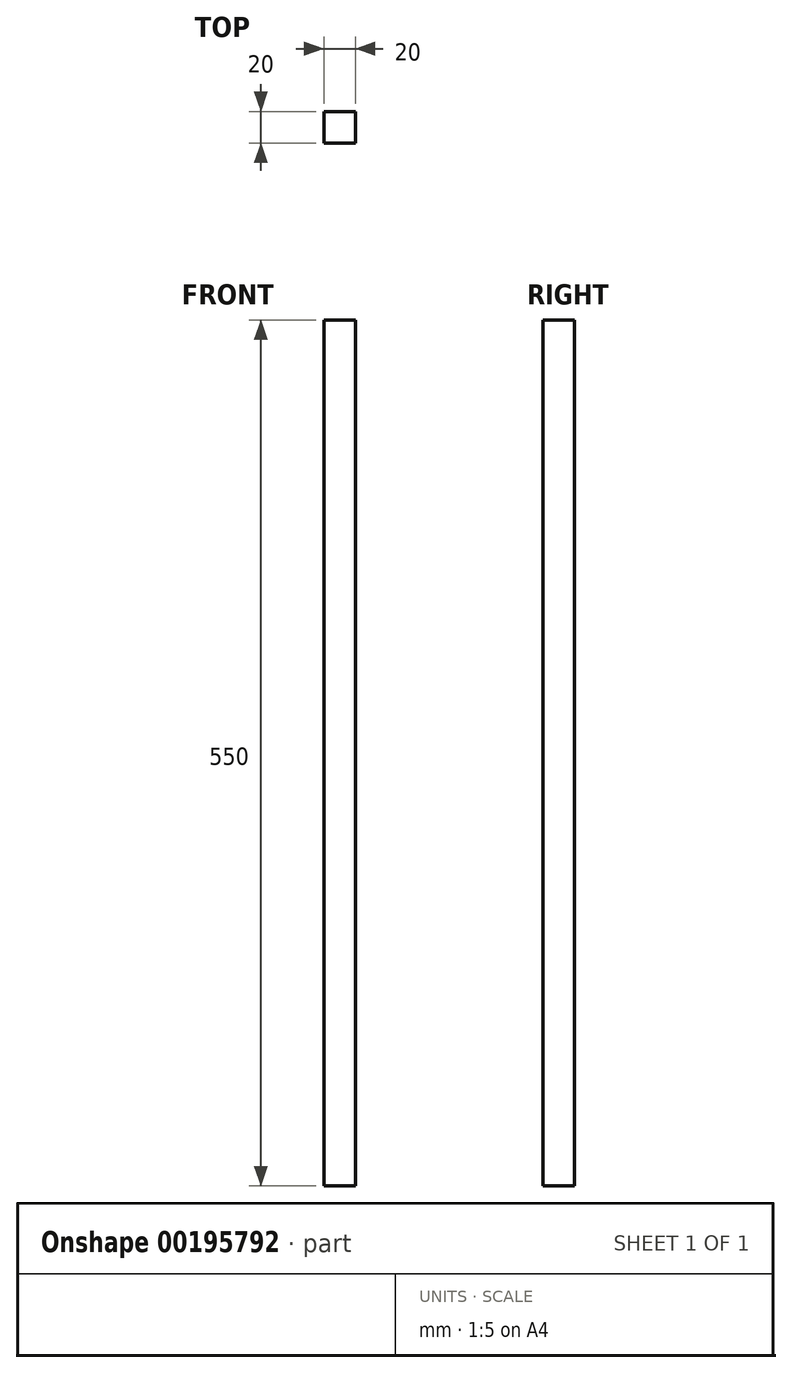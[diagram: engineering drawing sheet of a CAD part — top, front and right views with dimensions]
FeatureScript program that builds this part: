
annotation { "Feature Type Name" : "Feature", "Feature Type Description" : "" }
export const myFeature = defineFeature(function(context is Context, id is Id, definition is map)
    precondition{}
    {
        {
            var Q0;
            Q0=qCreatedBy(makeId("Top.planeOp"),FACE);
            var sketch = newSketch(context, id + "F0", { "sketchPlane" : qUnion([Q0])});
            skLineSegment(sketch, "E0.bottom", {"start": v(-86.76, -26.67) * mm, "end": v(-66.76, -26.67) * mm});
            skLineSegment(sketch, "E0.top", {"start": v(-86.76, -6.67) * mm, "end": v(-66.76, -6.67) * mm});
            skLineSegment(sketch, "E0.left", {"start": v(-86.76, -26.67) * mm, "end": v(-86.76, -6.67) * mm});
            skLineSegment(sketch, "E0.right", {"start": v(-66.76, -26.67) * mm, "end": v(-66.76, -6.67) * mm});
            skSolve(sketch);
        }
        {
            var Q0;
            Q0=makeQuery(id+"F0.imprint","IMPRINT",FACE,{"disambiguationData":[TD([[makeQuery(id+"F0.imprint","IMPRINT",EDGE,{"derivedFrom":sQuery(id+"F0.wireOp",EDGE,"E0.bottom")}),1.0]])]});
            extrude(context, id + "F1", {"entities" : qUnion([Q0]), "depth" : 550 * mm});
        }
    });
